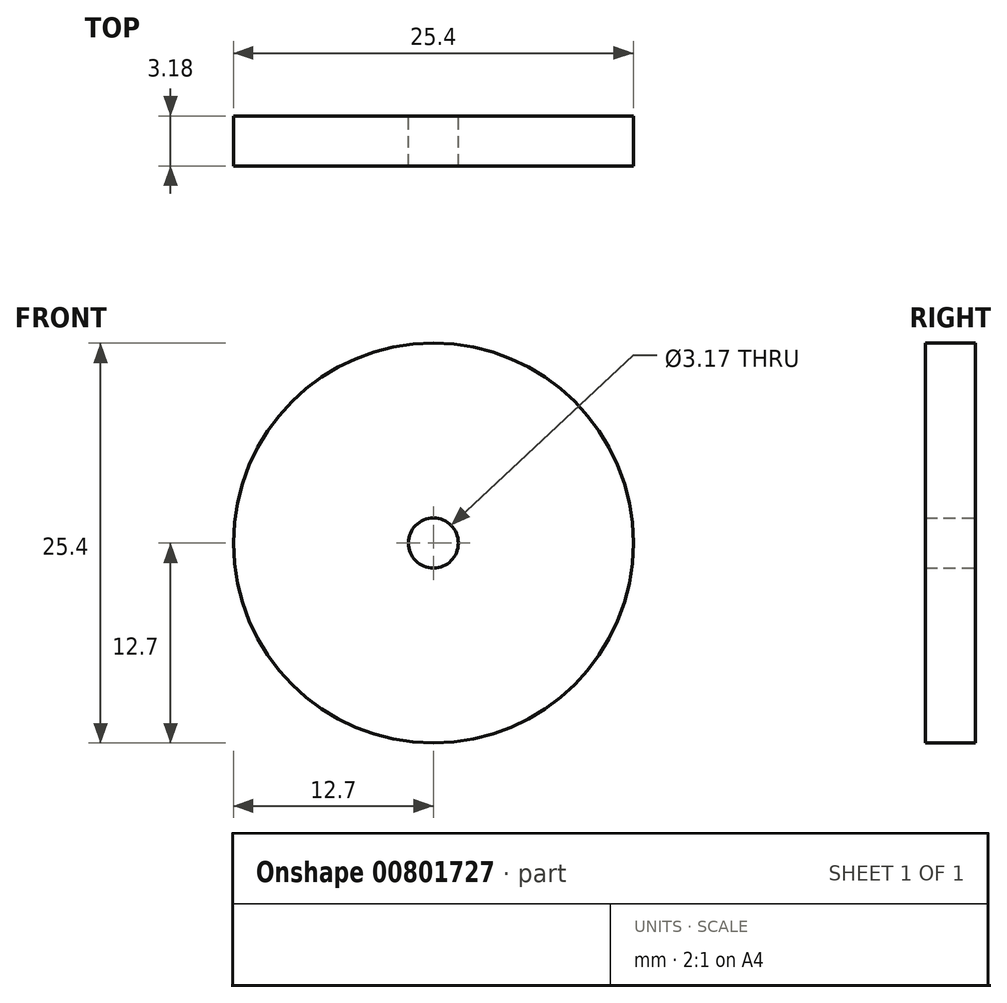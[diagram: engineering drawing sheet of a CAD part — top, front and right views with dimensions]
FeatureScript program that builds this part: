
annotation { "Feature Type Name" : "Feature", "Feature Type Description" : "" }
export const myFeature = defineFeature(function(context is Context, id is Id, definition is map)
    precondition{}
    {
        {
            var Q0;
            Q0=qCreatedBy(makeId("Front.planeOp"),FACE);
            var sketch = newSketch(context, id + "F0", { "sketchPlane" : qUnion([Q0])});
            skCircle(sketch, "E0", {"center": v(0, 0) * mm, "radius": 12.7 * mm});
            skCircle(sketch, "E1", {"center": v(0, 0) * mm, "radius": 1.59 * mm});
            skSolve(sketch);
        }
        {
            var Q0;
            Q0 = qSketchRegion(id + "F0", true);
            extrude(context, id + "F1", {"entities" : qUnion([Q0]), "depth" : 3.17 * mm, "offsetDistance" : 25.4 * mm});
        }
    });
